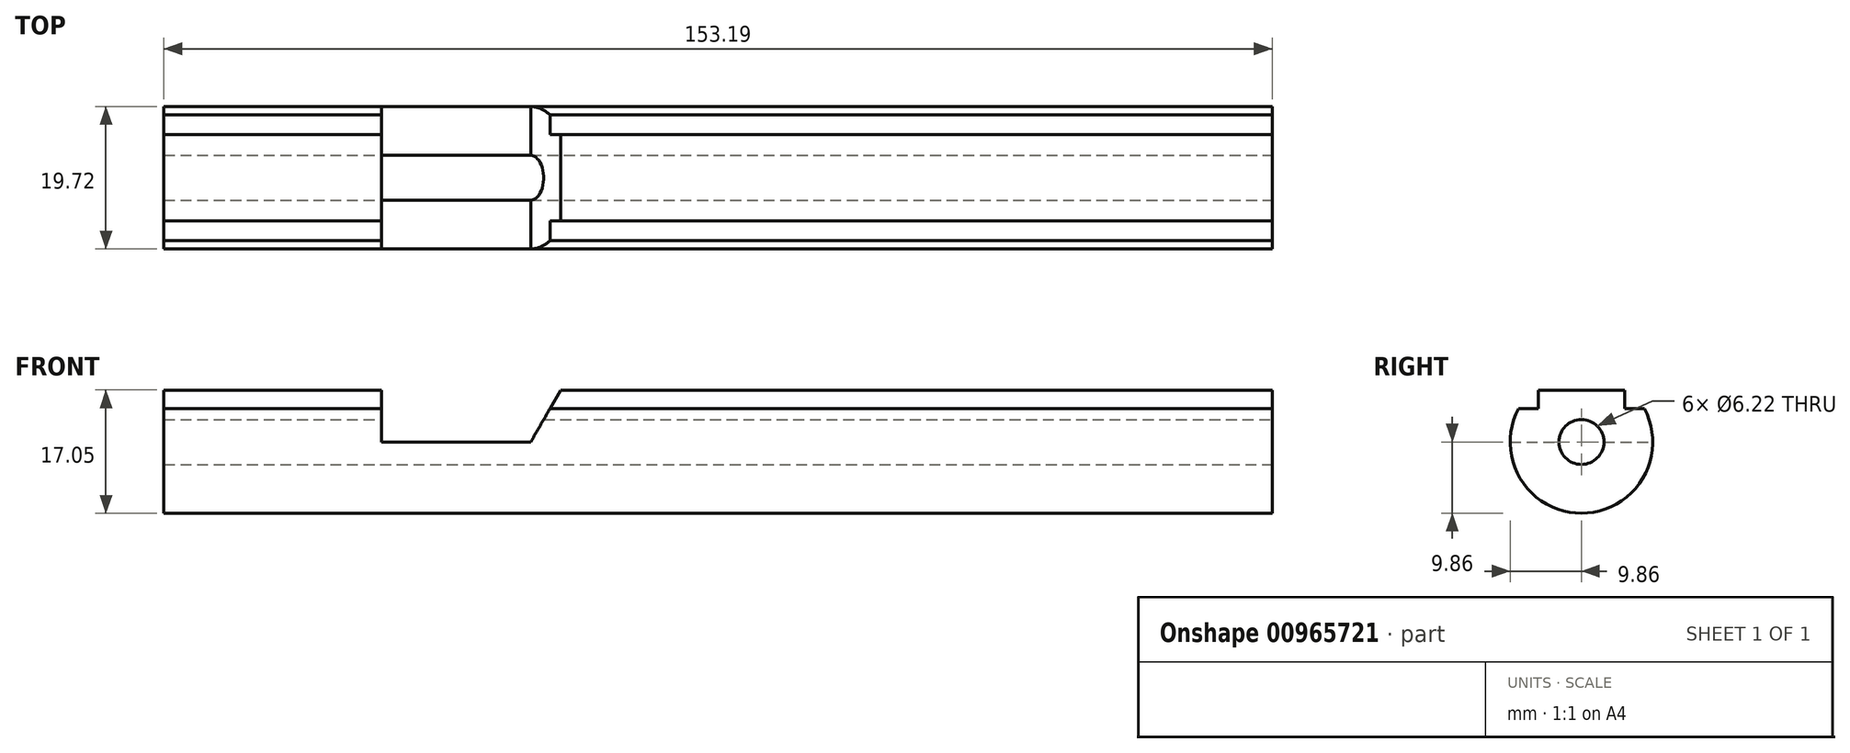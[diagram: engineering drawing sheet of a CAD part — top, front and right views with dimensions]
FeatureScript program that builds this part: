
annotation { "Feature Type Name" : "Feature", "Feature Type Description" : "" }
export const myFeature = defineFeature(function(context is Context, id is Id, definition is map)
    precondition{}
    {
        {
            var Q0;
            Q0=qCreatedBy(makeId("Right.planeOp"),FACE);
            var sketch = newSketch(context, id + "F0", { "sketchPlane" : qUnion([Q0])});
            skArc(sketch, "E0", {"start": v(-6.74, 7.19) * mm, "mid": v(0, -9.86) * mm, "end": v(6.74, 7.19) * mm});
            skLineSegment(sketch, "E1", {"start": v(-12.94, 0) * mm, "end": v(14.16, 0) * mm, "construction": true});
            skLineSegment(sketch, "E2.0", {"start": v(-6.74, 7.19) * mm, "end": v(6.74, 7.19) * mm});
            skSolve(sketch);
        }
        {
            var Q0;
            Q0=makeQuery(id+"F0.imprint","IMPRINT",FACE,{"disambiguationData":[TD([[makeQuery(id+"F0.imprint","IMPRINT",EDGE,{"derivedFrom":sQuery(id+"F0.wireOp",EDGE,"E0")}),1.0]])]});
            extrude(context, id + "F1", {"entities" : qUnion([Q0]), "oppositeDirection" : true, "depth" : 153.2 * mm, "offsetDistance" : 25.4 * mm});
        }
        {
            var Q0;
            Q0=qCreatedBy(makeId("Front.planeOp"),FACE);
            var sketch = newSketch(context, id + "F2", { "sketchPlane" : qUnion([Q0])});
            skLineSegment(sketch, "E3", {"start": v(-123.11, 9) * mm, "end": v(-123.11, 0) * mm});
            skLineSegment(sketch, "E4", {"start": v(-123.11, 0) * mm, "end": v(-102.49, 0) * mm});
            skLineSegment(sketch, "E5", {"start": v(-102.49, 0) * mm, "end": v(-97.29, 9) * mm});
            skLineSegment(sketch, "E6", {"start": v(-123.11, 9) * mm, "end": v(-97.29, 9) * mm});
            skSolve(sketch);
        }
        {
            var Q0;
            Q0 = qSketchRegion(id + "F2", true);
            extrude(context, id + "F3", {"entities" : qUnion([Q0]), "operationType" : NewBodyOperationType.REMOVE, "endBound" : BoundingType.SYMMETRIC, "depth" : 40.64 * mm, "offsetDistance" : 25.4 * mm});
        }
        {
            var Q0;
            Q0=makeQuery(id+"F1.opExtrude","CAP_FACE",FACE,{"disambiguationData":[OSD([sQuery(id+"F0.wireOp",EDGE,"E0"),sQuery(id+"F0.wireOp",EDGE,"E2.0")])],"isStart":true});
            var sketch = newSketch(context, id + "F4", { "sketchPlane" : qUnion([Q0])});
            skCircle(sketch, "E7", {"center": v(0, 0) * mm, "radius": 3.11 * mm});
            skSolve(sketch);
        }
        {
            var Q0;
            Q0 = qSketchRegion(id + "F4", true);
            extrude(context, id + "F5", {"entities" : qUnion([Q0]), "operationType" : NewBodyOperationType.REMOVE, "oppositeDirection" : true, "depth" : 170.7 * mm, "offsetDistance" : 25.4 * mm});
        }
        {
            var Q0;
            Q0=makeQuery(id+"F1.opExtrude","CAP_FACE",FACE,{"disambiguationData":[OSD([sQuery(id+"F0.wireOp",EDGE,"E0"),sQuery(id+"F0.wireOp",EDGE,"E2.0")])],"isStart":true});
            var sketch = newSketch(context, id + "F6", { "sketchPlane" : qUnion([Q0])});
            skLineSegment(sketch, "E8", {"start": v(0, 0) * mm, "end": v(0, 13.67) * mm, "construction": true});
            skLineSegment(sketch, "E9.0", {"start": v(5.97, 4.65) * mm, "end": v(5.97, 13.67) * mm});
            skLineSegment(sketch, "E10.MirrorCS", {"start": v(-5.97, 4.65) * mm, "end": v(-5.97, 13.67) * mm});
            skLineSegment(sketch, "E11.0", {"start": v(-9.23, 4.65) * mm, "end": v(-5.97, 4.65) * mm});
            skLineSegment(sketch, "E12.trimOffspring", {"start": v(5.97, 4.65) * mm, "end": v(9.2, 4.65) * mm});
            skPoint(sketch, "E13.orphan", {"position": v(5.97, 0) * mm});
            skPoint(sketch, "E14.orphan", {"position": v(-5.97, 0) * mm});
            skSolve(sketch);
        }
        {
            var Q0;
            {var subQ0=sQuery(id+"F6.wireOp",EDGE,"E11.0");var subQ1=sQuery(id+"F6.wireOp",EDGE,"E10.MirrorCS");var subQ2=makeQuery(id+"F6.imprint","INTERSECT",VERTEX,{"derivedFrom":[subQ1,subQ0]});Q0=makeQuery(id+"F6.imprint","IMPRINT",FACE,{"disambiguationData":[TD([[makeQuery(id+"F6.imprint","IMPRINT",EDGE,{"disambiguationData":[TD([[subQ2,-1.0]])],"derivedFrom":subQ1}),1.0]])]});}
            var Q1;
            {var subQ0=sQuery(id+"F6.wireOp",EDGE,"E12.trimOffspring");var subQ1=sQuery(id+"F6.wireOp",EDGE,"E9.0");var subQ2=makeQuery(id+"F6.imprint","INTERSECT",VERTEX,{"derivedFrom":[subQ1,subQ0]});Q1=makeQuery(id+"F6.imprint","IMPRINT",FACE,{"disambiguationData":[TD([[makeQuery(id+"F6.imprint","IMPRINT",EDGE,{"disambiguationData":[TD([[subQ2,-1.0]])],"derivedFrom":subQ1}),-1.0]])]});}
            extrude(context, id + "F7", {"entities" : qUnion([Q0, Q1]), "operationType" : NewBodyOperationType.REMOVE, "endBound" : BoundingType.THROUGH_ALL, "oppositeDirection" : true, "depth" : 25.4 * mm, "offsetDistance" : 25.4 * mm});
        }
        {
            var Q0;
            Q0=makeQuery(id+"F1.opExtrude","CAP_FACE",FACE,{"disambiguationData":[OSD([sQuery(id+"F0.wireOp",EDGE,"E0"),sQuery(id+"F0.wireOp",EDGE,"E2.0")])],"isStart":true});
            var sketch = newSketch(context, id + "F8", { "sketchPlane" : qUnion([Q0])});
            skCircle(sketch, "E15", {"center": v(0, 0) * mm, "radius": 15.88 * mm});
            skSolve(sketch);
        }
        {
            var Q0;
            Q0=makeQuery(id+"F8.imprint","IMPRINT",FACE,{"disambiguationData":[TD([[makeQuery(id+"F8.imprint","IMPRINT",EDGE,{"derivedFrom":sQuery(id+"F8.wireOp",EDGE,"E15")}),1.0]])]});
            extrude(context, id + "F9", {"entities" : qUnion([Q0]), "depth" : 50.8 * mm, "offsetDistance" : 25.4 * mm});
        }
        {
            var Q0;
            Q0=makeQuery(id+"F9.opExtrude","SWEPT_BODY",BODY,{"disambiguationData":[OSD([sQuery(id+"F0.wireOp",EDGE,"E0"),sQuery(id+"F0.wireOp",EDGE,"E2.0"),sQuery(id+"F6.wireOp",EDGE,"E9.0"),sQuery(id+"F6.wireOp",EDGE,"E10.MirrorCS"),sQuery(id+"F6.wireOp",EDGE,"E11.0"),sQuery(id+"F6.wireOp",EDGE,"E12.trimOffspring"),sQuery(id+"F8.wireOp",EDGE,"E15")])]});
            deleteBodies(context, id + "F10", {"entities" : qUnion([Q0])});
        }
    });
